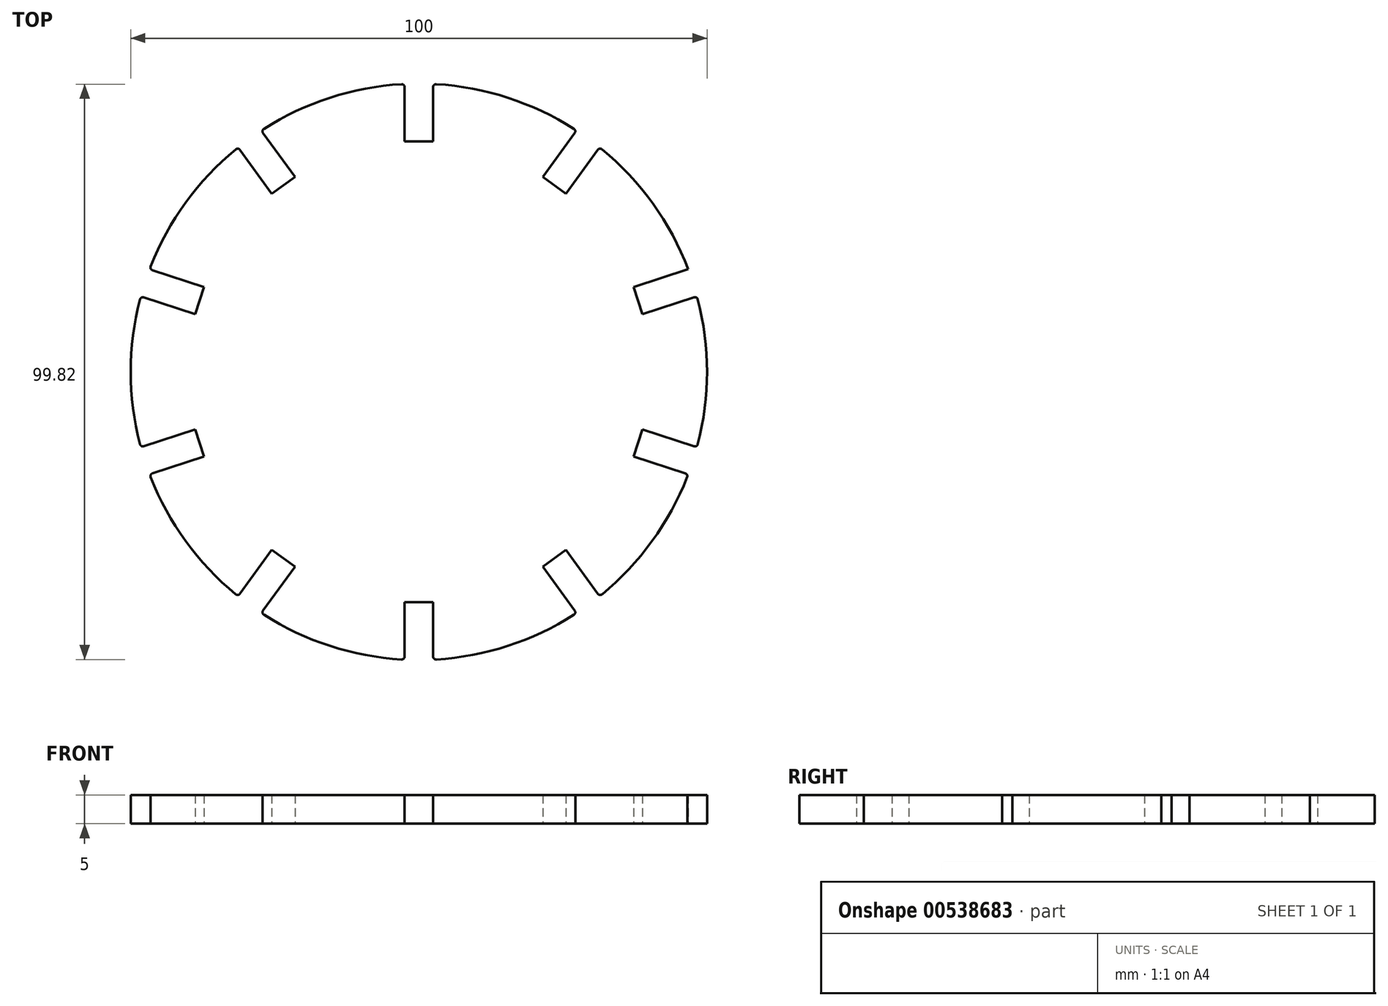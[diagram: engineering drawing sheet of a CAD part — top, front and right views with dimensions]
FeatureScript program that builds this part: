
annotation { "Feature Type Name" : "Feature", "Feature Type Description" : "" }
export const myFeature = defineFeature(function(context is Context, id is Id, definition is map)
    precondition{}
    {
        {
            var Q0;
            Q0=qCreatedBy(makeId("Top.planeOp"),FACE);
            var sketch = newSketch(context, id + "F0", { "sketchPlane" : qUnion([Q0])});
            skArc(sketch, "E0", {"start": v(-31.77, 38.61) * mm, "mid": v(-40.45, 29.39) * mm, "end": v(-46.54, 18.28) * mm});
            skLineSegment(sketch, "E1", {"start": v(0, 50) * mm, "end": v(0, -44.22) * mm, "construction": true});
            skLineSegment(sketch, "E2.0", {"start": v(-2.48, 38.51) * mm, "end": v(-2.47, -44.22) * mm, "construction": true});
            skLineSegment(sketch, "E3.0", {"start": v(2.47, 38.51) * mm, "end": v(2.48, -44.22) * mm, "construction": true});
            skLineSegment(sketch, "E4", {"start": v(-34.48, 40) * mm, "end": v(34.48, 40) * mm, "construction": true});
            skLineSegment(sketch, "E5", {"start": v(-2.48, 49.41) * mm, "end": v(-2.48, 40) * mm});
            skLineSegment(sketch, "E6", {"start": v(-2.48, 40) * mm, "end": v(2.48, 40) * mm});
            skLineSegment(sketch, "E7", {"start": v(2.47, 40) * mm, "end": v(2.47, 49.41) * mm});
            skLineSegment(sketch, "E8.1.0", {"start": v(-31.05, 38.52) * mm, "end": v(-25.51, 30.9) * mm});
            skLineSegment(sketch, "E8.1.1", {"start": v(-25.51, 30.9) * mm, "end": v(-21.5, 33.82) * mm});
            skLineSegment(sketch, "E8.1.2", {"start": v(-21.5, 33.82) * mm, "end": v(-27.04, 41.43) * mm});
            skLineSegment(sketch, "E8.2.0", {"start": v(-47.76, 12.91) * mm, "end": v(-38.8, 10) * mm});
            skLineSegment(sketch, "E8.2.1", {"start": v(-38.8, 10) * mm, "end": v(-37.28, 14.71) * mm});
            skLineSegment(sketch, "E8.2.2", {"start": v(-37.28, 14.71) * mm, "end": v(-46.23, 17.62) * mm});
            skLineSegment(sketch, "E8.3.0", {"start": v(-46.23, -17.62) * mm, "end": v(-37.28, -14.71) * mm});
            skLineSegment(sketch, "E8.3.1", {"start": v(-37.28, -14.71) * mm, "end": v(-38.8, -10) * mm});
            skLineSegment(sketch, "E8.3.2", {"start": v(-38.8, -10) * mm, "end": v(-47.76, -12.91) * mm});
            skLineSegment(sketch, "E8.4.0", {"start": v(-27.04, -41.43) * mm, "end": v(-21.5, -33.82) * mm});
            skLineSegment(sketch, "E8.4.1", {"start": v(-21.5, -33.82) * mm, "end": v(-25.51, -30.9) * mm});
            skLineSegment(sketch, "E8.4.2", {"start": v(-25.51, -30.9) * mm, "end": v(-31.05, -38.52) * mm});
            skLineSegment(sketch, "E8.5.0", {"start": v(2.47, -49.41) * mm, "end": v(2.47, -40) * mm});
            skLineSegment(sketch, "E8.5.1", {"start": v(2.47, -40) * mm, "end": v(-2.48, -40) * mm});
            skLineSegment(sketch, "E8.5.2", {"start": v(-2.48, -40) * mm, "end": v(-2.48, -49.41) * mm});
            skLineSegment(sketch, "E8.6.0", {"start": v(31.05, -38.52) * mm, "end": v(25.51, -30.9) * mm});
            skLineSegment(sketch, "E8.6.1", {"start": v(25.51, -30.9) * mm, "end": v(21.5, -33.82) * mm});
            skLineSegment(sketch, "E8.6.2", {"start": v(21.5, -33.82) * mm, "end": v(27.04, -41.43) * mm});
            skLineSegment(sketch, "E8.7.0", {"start": v(47.76, -12.91) * mm, "end": v(38.8, -10) * mm});
            skLineSegment(sketch, "E8.7.1", {"start": v(38.8, -10) * mm, "end": v(37.28, -14.71) * mm});
            skLineSegment(sketch, "E8.7.2", {"start": v(37.28, -14.71) * mm, "end": v(46.23, -17.62) * mm});
            skLineSegment(sketch, "E8.8.0", {"start": v(46.73, 17.79) * mm, "end": v(37.28, 14.71) * mm});
            skLineSegment(sketch, "E8.8.1", {"start": v(37.28, 14.71) * mm, "end": v(38.8, 10) * mm});
            skLineSegment(sketch, "E8.8.2", {"start": v(38.8, 10) * mm, "end": v(47.76, 12.91) * mm});
            skLineSegment(sketch, "E8.9.0", {"start": v(27.04, 41.43) * mm, "end": v(21.5, 33.82) * mm});
            skLineSegment(sketch, "E8.9.1", {"start": v(21.5, 33.82) * mm, "end": v(25.51, 30.9) * mm});
            skLineSegment(sketch, "E8.9.2", {"start": v(25.51, 30.9) * mm, "end": v(31.05, 38.52) * mm});
            skArc(sketch, "E9.trimOffspring", {"start": v(-48.4, 12.56) * mm, "mid": v(-50, 0) * mm, "end": v(-48.4, -12.56) * mm});
            skArc(sketch, "E10.trimOffspring", {"start": v(-46.54, -18.28) * mm, "mid": v(-40.45, -29.39) * mm, "end": v(-31.77, -38.61) * mm});
            skArc(sketch, "E11.trimOffspring", {"start": v(-26.9, -42.14) * mm, "mid": v(-15.45, -47.55) * mm, "end": v(-3, -49.9) * mm});
            skArc(sketch, "E12.trimOffspring", {"start": v(3, -49.9) * mm, "mid": v(15.45, -47.55) * mm, "end": v(26.9, -42.14) * mm});
            skArc(sketch, "E13.trimOffspring", {"start": v(31.77, -38.61) * mm, "mid": v(40.45, -29.39) * mm, "end": v(46.54, -18.28) * mm});
            skArc(sketch, "E14.trimOffspring", {"start": v(48.4, -12.56) * mm, "mid": v(50, 0) * mm, "end": v(48.4, 12.56) * mm});
            skArc(sketch, "E15.trimOffspring", {"start": v(46.73, 17.79) * mm, "mid": v(40.6, 29.17) * mm, "end": v(31.77, 38.61) * mm});
            skArc(sketch, "E16.trimOffspring", {"start": v(26.9, 42.14) * mm, "mid": v(15.45, 47.55) * mm, "end": v(3, 49.9) * mm});
            skArc(sketch, "E17.trimOffspring", {"start": v(-3, 49.9) * mm, "mid": v(-15.45, 47.55) * mm, "end": v(-26.9, 42.14) * mm});
            skPoint(sketch, "E18.visualSharp", {"position": v(-31.36, 38.95) * mm});
            skArc(sketch, "E18.filletArc", {"start": v(-31.05, 38.52) * mm, "mid": v(-31.39, 38.72) * mm, "end": v(-31.77, 38.61) * mm});
            skPoint(sketch, "E19.visualSharp", {"position": v(-46.73, 17.79) * mm});
            skArc(sketch, "E19.filletArc", {"start": v(-46.54, 18.28) * mm, "mid": v(-46.52, 17.88) * mm, "end": v(-46.23, 17.62) * mm});
            skPoint(sketch, "E20.visualSharp", {"position": v(-48.26, 13.08) * mm});
            skArc(sketch, "E20.filletArc", {"start": v(-47.76, 12.91) * mm, "mid": v(-48.15, 12.88) * mm, "end": v(-48.4, 12.56) * mm});
            skPoint(sketch, "E21.visualSharp", {"position": v(-48.26, -13.08) * mm});
            skArc(sketch, "E21.filletArc", {"start": v(-48.4, -12.56) * mm, "mid": v(-48.15, -12.88) * mm, "end": v(-47.76, -12.91) * mm});
            skPoint(sketch, "E22.visualSharp", {"position": v(-46.73, -17.79) * mm});
            skArc(sketch, "E22.filletArc", {"start": v(-46.23, -17.62) * mm, "mid": v(-46.52, -17.88) * mm, "end": v(-46.54, -18.28) * mm});
            skPoint(sketch, "E23.visualSharp", {"position": v(-31.36, -38.95) * mm});
            skArc(sketch, "E23.filletArc", {"start": v(-31.77, -38.61) * mm, "mid": v(-31.39, -38.72) * mm, "end": v(-31.05, -38.52) * mm});
            skPoint(sketch, "E24.visualSharp", {"position": v(-27.35, -41.86) * mm});
            skArc(sketch, "E24.filletArc", {"start": v(-27.04, -41.43) * mm, "mid": v(-27.13, -41.82) * mm, "end": v(-26.9, -42.14) * mm});
            skPoint(sketch, "E25.visualSharp", {"position": v(-2.48, -49.94) * mm});
            skArc(sketch, "E25.filletArc", {"start": v(-3, -49.9) * mm, "mid": v(-2.63, -49.77) * mm, "end": v(-2.48, -49.41) * mm});
            skPoint(sketch, "E26.visualSharp", {"position": v(2.47, -49.94) * mm});
            skArc(sketch, "E26.filletArc", {"start": v(2.47, -49.41) * mm, "mid": v(2.63, -49.77) * mm, "end": v(3, -49.9) * mm});
            skPoint(sketch, "E27.visualSharp", {"position": v(27.35, -41.86) * mm});
            skArc(sketch, "E27.filletArc", {"start": v(26.9, -42.14) * mm, "mid": v(27.13, -41.82) * mm, "end": v(27.04, -41.43) * mm});
            skPoint(sketch, "E28.visualSharp", {"position": v(31.36, -38.95) * mm});
            skArc(sketch, "E28.filletArc", {"start": v(31.05, -38.52) * mm, "mid": v(31.39, -38.72) * mm, "end": v(31.77, -38.61) * mm});
            skPoint(sketch, "E29.visualSharp", {"position": v(46.73, -17.79) * mm});
            skArc(sketch, "E29.filletArc", {"start": v(46.54, -18.28) * mm, "mid": v(46.52, -17.88) * mm, "end": v(46.23, -17.62) * mm});
            skPoint(sketch, "E30.visualSharp", {"position": v(48.26, -13.08) * mm});
            skArc(sketch, "E30.filletArc", {"start": v(47.76, -12.91) * mm, "mid": v(48.15, -12.88) * mm, "end": v(48.4, -12.56) * mm});
            skPoint(sketch, "E31.visualSharp", {"position": v(48.26, 13.08) * mm});
            skArc(sketch, "E31.filletArc", {"start": v(48.4, 12.56) * mm, "mid": v(48.15, 12.88) * mm, "end": v(47.76, 12.91) * mm});
            skPoint(sketch, "E32.visualSharp", {"position": v(31.36, 38.95) * mm});
            skArc(sketch, "E32.filletArc", {"start": v(31.77, 38.61) * mm, "mid": v(31.39, 38.72) * mm, "end": v(31.05, 38.52) * mm});
            skPoint(sketch, "E33.visualSharp", {"position": v(27.35, 41.86) * mm});
            skArc(sketch, "E33.filletArc", {"start": v(27.04, 41.43) * mm, "mid": v(27.13, 41.82) * mm, "end": v(26.9, 42.14) * mm});
            skPoint(sketch, "E34.visualSharp", {"position": v(2.48, 49.94) * mm});
            skArc(sketch, "E34.filletArc", {"start": v(3, 49.9) * mm, "mid": v(2.63, 49.77) * mm, "end": v(2.48, 49.41) * mm});
            skPoint(sketch, "E35.visualSharp", {"position": v(-2.48, 49.94) * mm});
            skArc(sketch, "E35.filletArc", {"start": v(-2.47, 49.41) * mm, "mid": v(-2.63, 49.77) * mm, "end": v(-3, 49.9) * mm});
            skPoint(sketch, "E36.visualSharp", {"position": v(-27.35, 41.86) * mm});
            skArc(sketch, "E36.filletArc", {"start": v(-26.9, 42.14) * mm, "mid": v(-27.13, 41.82) * mm, "end": v(-27.04, 41.43) * mm});
            skSolve(sketch);
        }
        {
            var Q0;
            Q0=makeQuery(id+"F0.imprint","IMPRINT",FACE,{"disambiguationData":[TD([[makeQuery(id+"F0.imprint","IMPRINT",EDGE,{"derivedFrom":sQuery(id+"F0.wireOp",EDGE,"E0")}),1.0]])]});
            extrude(context, id + "F1", {"entities" : qUnion([Q0]), "depth" : 5 * mm, "offsetDistance" : 25 * mm});
        }
    });
